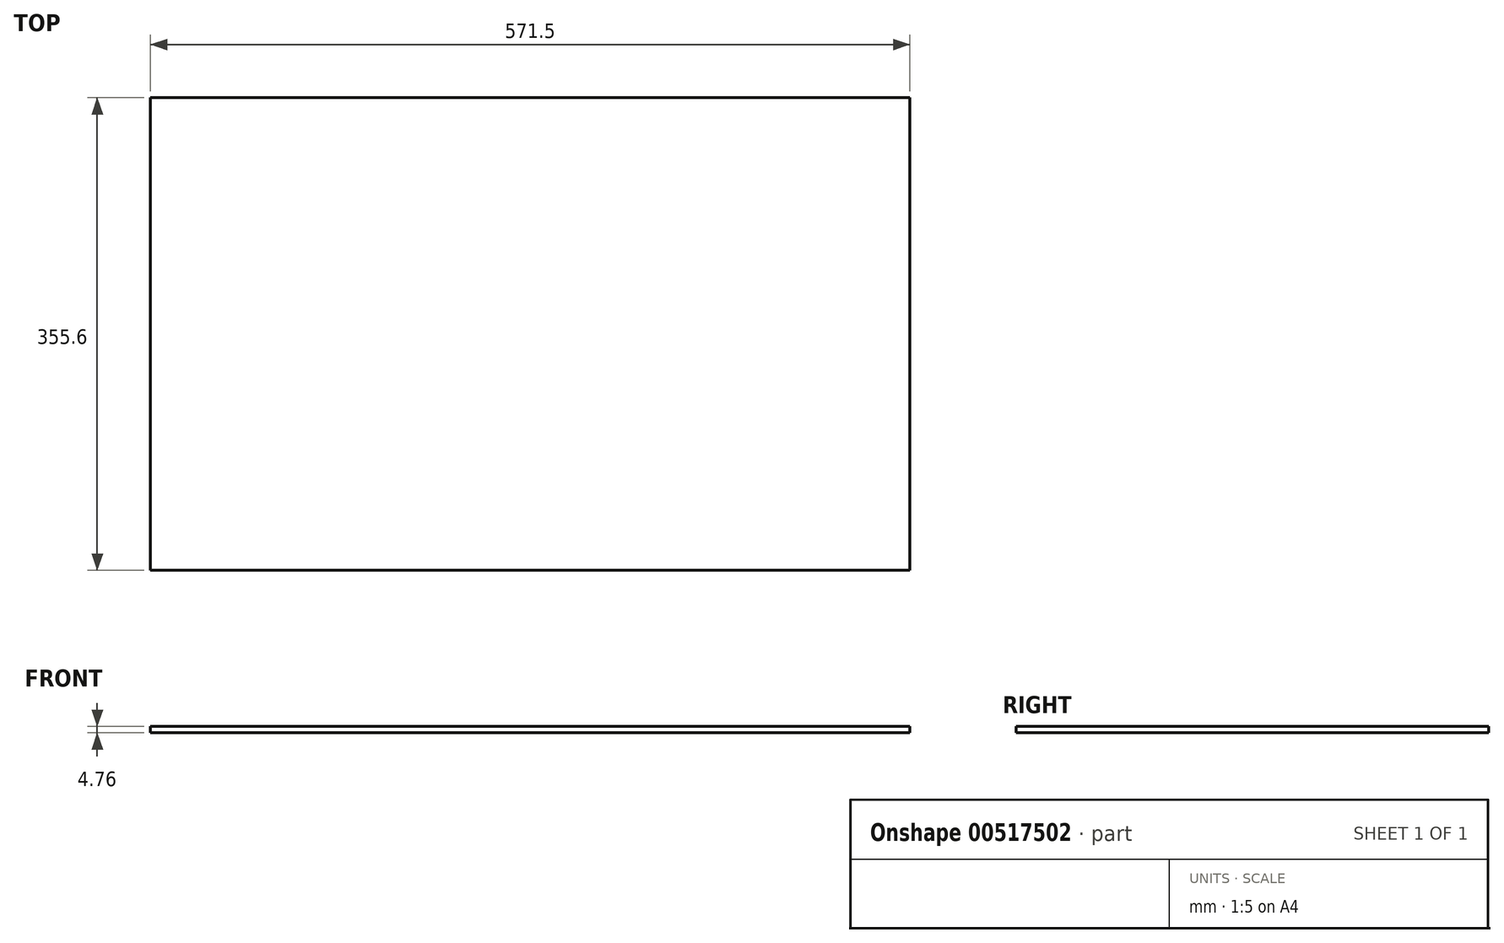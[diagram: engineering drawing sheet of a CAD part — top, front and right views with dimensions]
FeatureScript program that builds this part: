
annotation { "Feature Type Name" : "Feature", "Feature Type Description" : "" }
export const myFeature = defineFeature(function(context is Context, id is Id, definition is map)
    precondition{}
    {
        {
            var Q0;
            Q0=qCreatedBy(makeId("Top.planeOp"),FACE);
            var sketch = newSketch(context, id + "F0", { "sketchPlane" : qUnion([Q0])});
            skLineSegment(sketch, "E0.bottom", {"start": v(-285.75, 177.8) * mm, "end": v(285.75, 177.8) * mm});
            skLineSegment(sketch, "E0.top", {"start": v(-285.75, -177.8) * mm, "end": v(285.75, -177.8) * mm});
            skLineSegment(sketch, "E0.left", {"start": v(-285.75, 177.8) * mm, "end": v(-285.75, -177.8) * mm});
            skLineSegment(sketch, "E0.right", {"start": v(285.75, 177.8) * mm, "end": v(285.75, -177.8) * mm});
            skPoint(sketch, "E0.middle", {"position": v(0, 0) * mm});
            skSolve(sketch);
        }
        {
            var Q0;
            Q0 = qSketchRegion(id + "F0", true);
            extrude(context, id + "F1", {"entities" : qUnion([Q0]), "depth" : 4.76 * mm, "offsetDistance" : 25.4 * mm});
        }
    });
